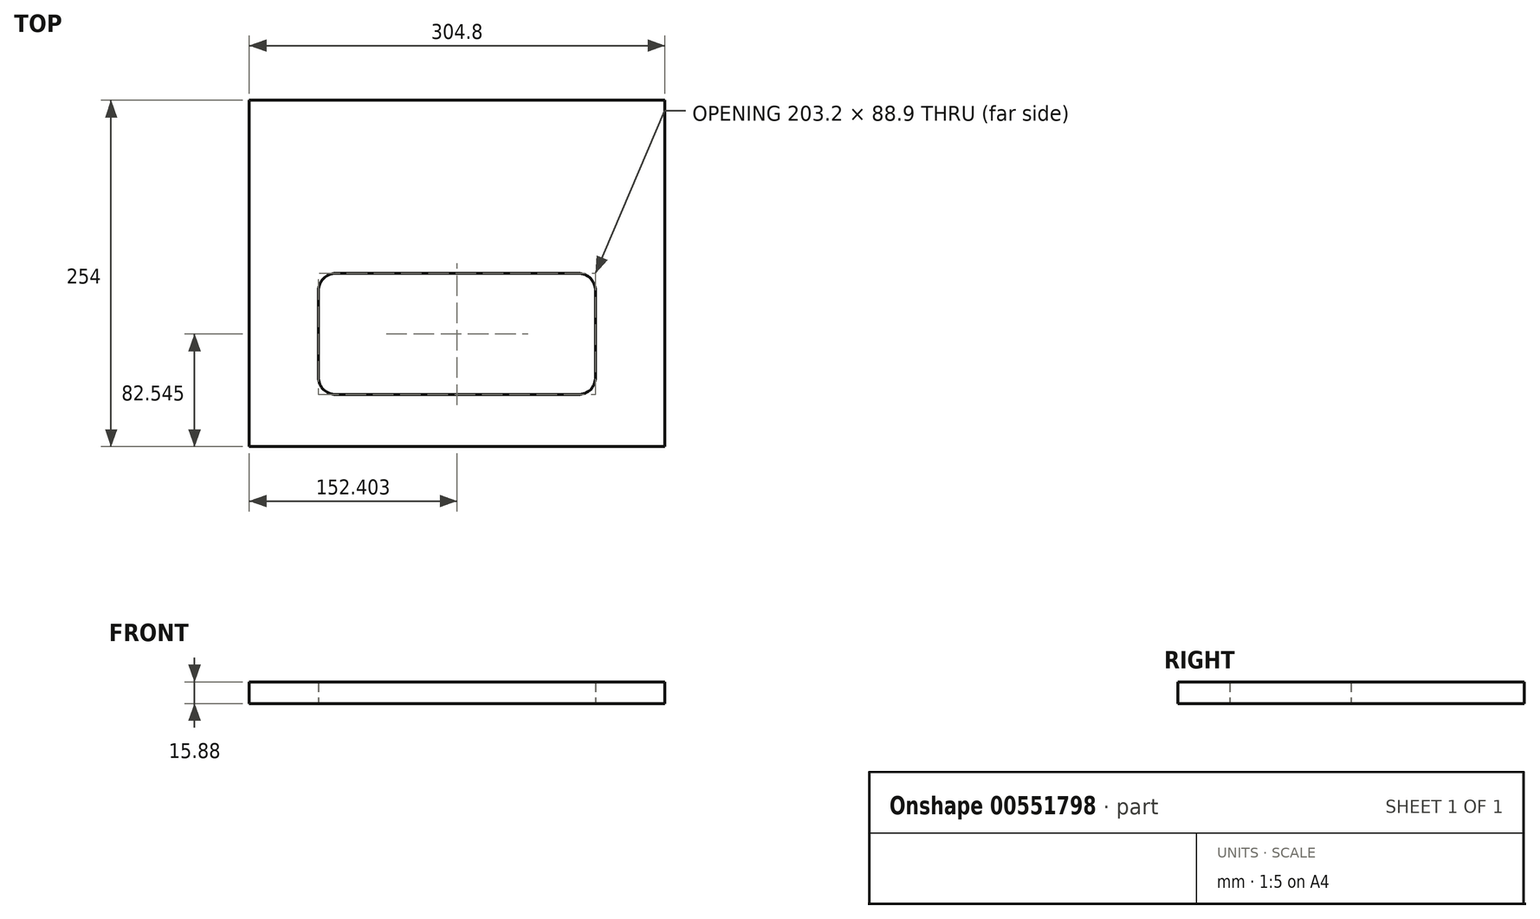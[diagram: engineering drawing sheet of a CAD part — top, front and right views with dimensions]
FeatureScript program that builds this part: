
annotation { "Feature Type Name" : "Feature", "Feature Type Description" : "" }
export const myFeature = defineFeature(function(context is Context, id is Id, definition is map)
    precondition{}
    {
        {
            var Q0;
            Q0=qCreatedBy(makeId("Top.planeOp"),FACE);
            var sketch = newSketch(context, id + "F0", { "sketchPlane" : qUnion([Q0])});
            skLineSegment(sketch, "E0.bottom", {"start": v(-422.17, 153.6) * mm, "end": v(-117.37, 153.6) * mm});
            skLineSegment(sketch, "E0.top", {"start": v(-422.17, -100.4) * mm, "end": v(-117.37, -100.4) * mm});
            skLineSegment(sketch, "E0.left", {"start": v(-422.17, 153.6) * mm, "end": v(-422.17, -100.4) * mm});
            skLineSegment(sketch, "E0.right", {"start": v(-117.37, 153.6) * mm, "end": v(-117.37, -100.4) * mm});
            skLineSegment(sketch, "E1.bottom", {"start": v(-358.67, 26.6) * mm, "end": v(-180.87, 26.6) * mm});
            skLineSegment(sketch, "E1.top", {"start": v(-358.67, -62.3) * mm, "end": v(-180.87, -62.3) * mm});
            skLineSegment(sketch, "E1.left", {"start": v(-371.37, 13.9) * mm, "end": v(-371.37, -49.6) * mm});
            skLineSegment(sketch, "E1.right", {"start": v(-168.17, 13.9) * mm, "end": v(-168.17, -49.6) * mm});
            skPoint(sketch, "E2.visualSharp", {"position": v(-371.37, 26.6) * mm});
            skArc(sketch, "E2.filletArc", {"start": v(-358.67, 26.6) * mm, "mid": v(-367.65, 22.89) * mm, "end": v(-371.37, 13.9) * mm});
            skPoint(sketch, "E3.visualSharp", {"position": v(-168.17, 26.6) * mm});
            skArc(sketch, "E3.filletArc", {"start": v(-168.17, 13.9) * mm, "mid": v(-171.89, 22.89) * mm, "end": v(-180.87, 26.6) * mm});
            skPoint(sketch, "E4.visualSharp", {"position": v(-168.17, -62.3) * mm});
            skArc(sketch, "E4.filletArc", {"start": v(-180.87, -62.3) * mm, "mid": v(-171.89, -58.58) * mm, "end": v(-168.17, -49.6) * mm});
            skPoint(sketch, "E5.visualSharp", {"position": v(-371.37, -62.3) * mm});
            skArc(sketch, "E5.filletArc", {"start": v(-371.37, -49.6) * mm, "mid": v(-367.65, -58.58) * mm, "end": v(-358.67, -62.3) * mm});
            skPoint(sketch, "E6", {"position": v(-168.17, -17.84) * mm});
            skPoint(sketch, "E7", {"position": v(-117.37, -17.84) * mm});
            skPoint(sketch, "E8", {"position": v(-269.77, 153.6) * mm});
            skPoint(sketch, "E9", {"position": v(-269.77, 26.6) * mm});
            skPoint(sketch, "E10", {"position": v(-269.77, -62.3) * mm});
            skPoint(sketch, "E11", {"position": v(-269.77, -100.4) * mm});
            skPoint(sketch, "E12", {"position": v(-371.37, -17.84) * mm});
            skPoint(sketch, "E13", {"position": v(-422.17, -17.84) * mm});
            skSolve(sketch);
        }
        {
            var Q0;
            Q0 = qSketchRegion(id + "F0", true);
            extrude(context, id + "F1", {"entities" : qUnion([Q0]), "depth" : 15.88 * mm, "offsetDistance" : 25.4 * mm});
        }
    });
